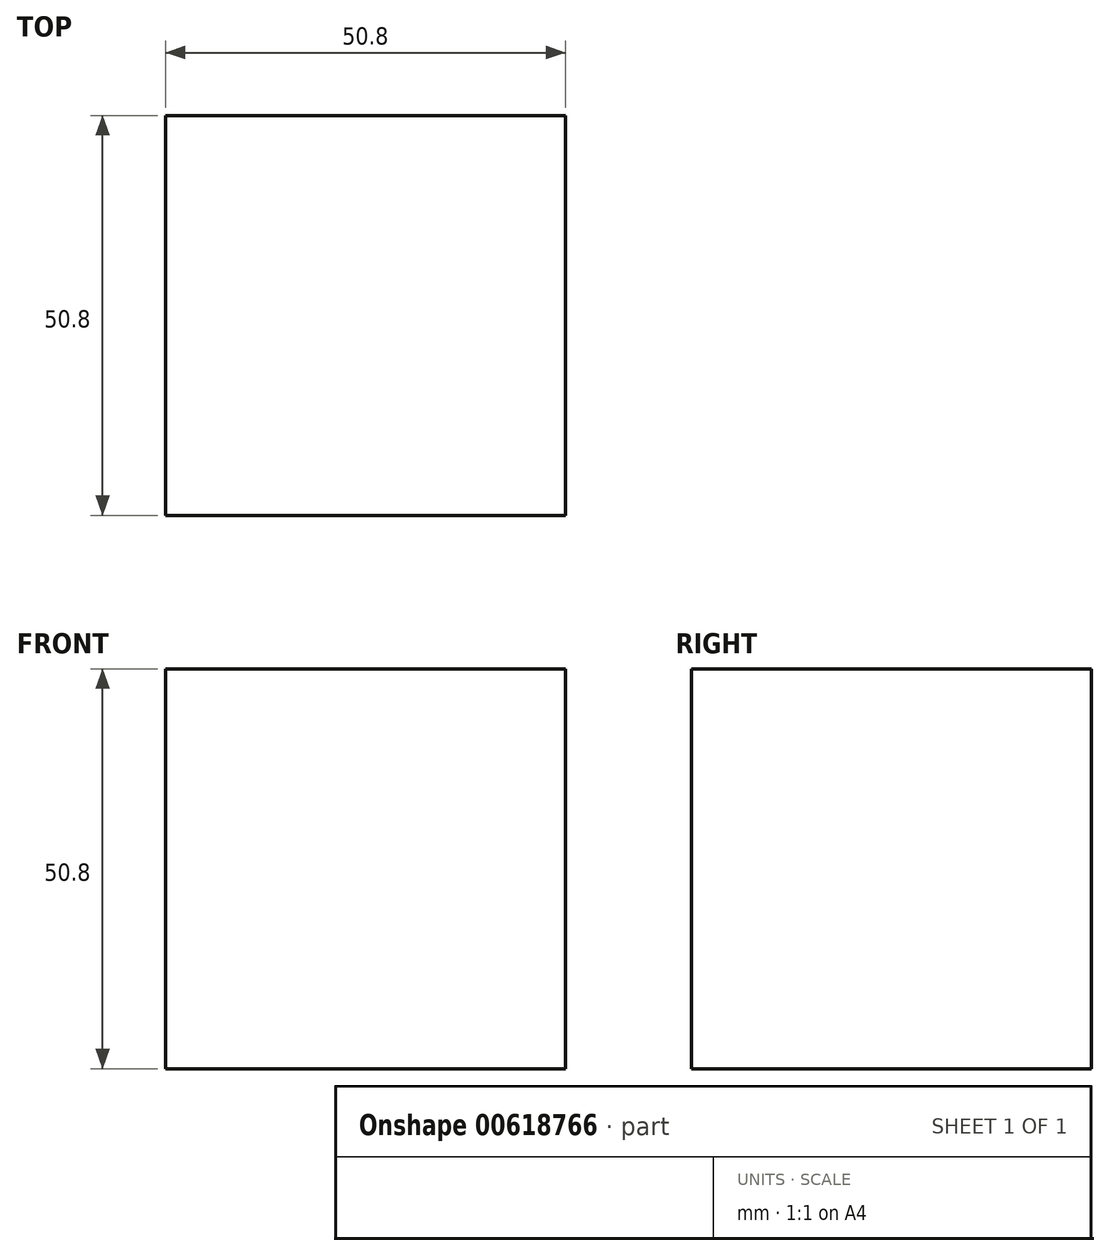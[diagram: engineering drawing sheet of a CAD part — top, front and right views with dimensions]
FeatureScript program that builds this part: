
annotation { "Feature Type Name" : "Feature", "Feature Type Description" : "" }
export const myFeature = defineFeature(function(context is Context, id is Id, definition is map)
    precondition{}
    {
        {
            var Q0;
            Q0=qCreatedBy(makeId("Top.planeOp"),FACE);
            var sketch = newSketch(context, id + "F0", { "sketchPlane" : qUnion([Q0])});
            skLineSegment(sketch, "E0.bottom", {"start": v(25.4, 25.4) * mm, "end": v(-25.4, 25.4) * mm});
            skLineSegment(sketch, "E0.top", {"start": v(25.4, -25.4) * mm, "end": v(-25.4, -25.4) * mm});
            skLineSegment(sketch, "E0.left", {"start": v(25.4, 25.4) * mm, "end": v(25.4, -25.4) * mm});
            skLineSegment(sketch, "E0.right", {"start": v(-25.4, 25.4) * mm, "end": v(-25.4, -25.4) * mm});
            skPoint(sketch, "E0.middle", {"position": v(0, 0) * mm});
            skSolve(sketch);
        }
        {
            var Q0;
            Q0 = qSketchRegion(id + "F0", true);
            extrude(context, id + "F1", {"entities" : qUnion([Q0]), "depth" : 50.8 * mm, "offsetDistance" : 25.4 * mm});
        }
    });
